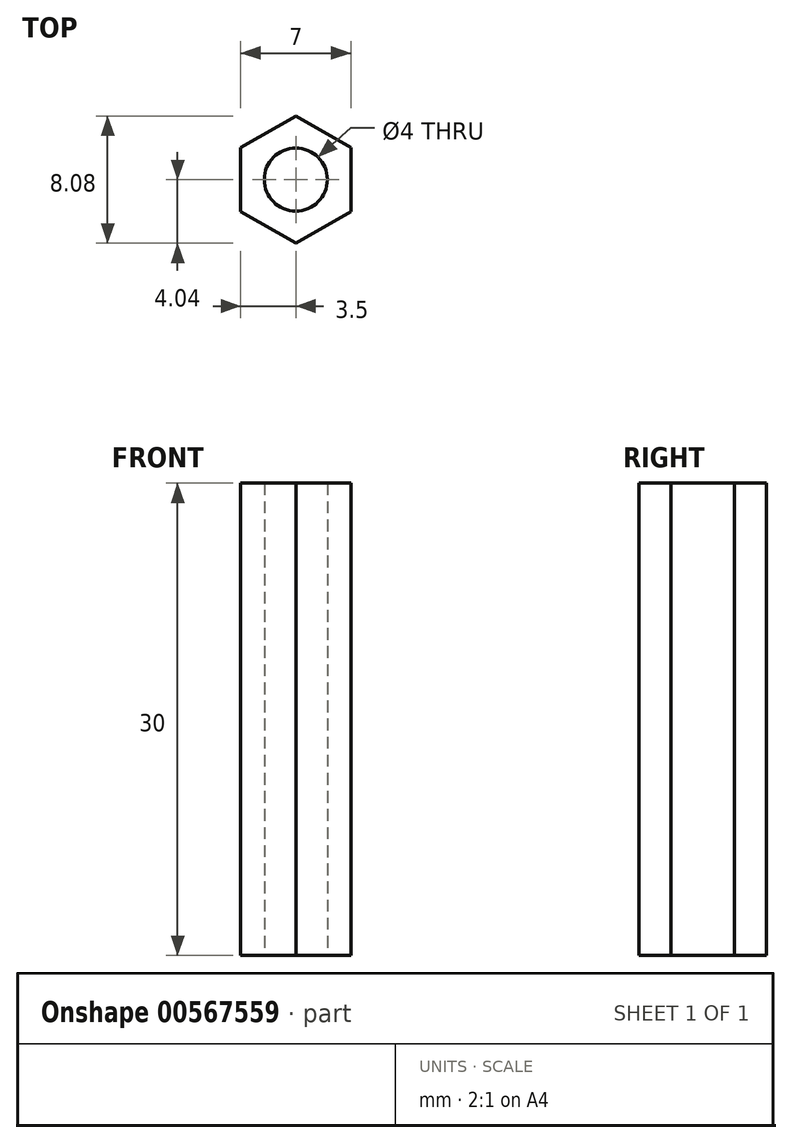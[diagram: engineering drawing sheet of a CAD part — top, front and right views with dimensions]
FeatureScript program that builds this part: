
annotation { "Feature Type Name" : "Feature", "Feature Type Description" : "" }
export const myFeature = defineFeature(function(context is Context, id is Id, definition is map)
    precondition{}
    {
        {
            var Q0;
            Q0=qCreatedBy(makeId("Top.planeOp"),FACE);
            var sketch = newSketch(context, id + "F0", { "sketchPlane" : qUnion([Q0])});
            skCircle(sketch, "E0.cCircle", {"center": v(0, 0) * mm, "radius": 3.5 * mm, "construction": true});
            skLineSegment(sketch, "E0.0", {"start": v(3.5, -2.02) * mm, "end": v(0, -4.04) * mm});
            skLineSegment(sketch, "E0.1", {"start": v(0, -4.04) * mm, "end": v(-3.5, -2.02) * mm});
            skLineSegment(sketch, "E0.2", {"start": v(-3.5, -2.02) * mm, "end": v(-3.5, 2.02) * mm});
            skLineSegment(sketch, "E0.3", {"start": v(-3.5, 2.02) * mm, "end": v(0, 4.04) * mm});
            skLineSegment(sketch, "E0.4", {"start": v(0, 4.04) * mm, "end": v(3.5, 2.02) * mm});
            skLineSegment(sketch, "E0.5", {"start": v(3.5, 2.02) * mm, "end": v(3.5, -2.02) * mm});
            skPoint(sketch, "E0.0.midPoint", {"position": v(1.75, -3.03) * mm});
            skCircle(sketch, "E1", {"center": v(0, 0) * mm, "radius": 2 * mm});
            skSolve(sketch);
        }
        {
            var Q0;
            Q0 = qSketchRegion(id + "F0", true);
            extrude(context, id + "F1", {"entities" : qUnion([Q0]), "depth" : 30 * mm, "offsetDistance" : 25 * mm});
        }
    });
